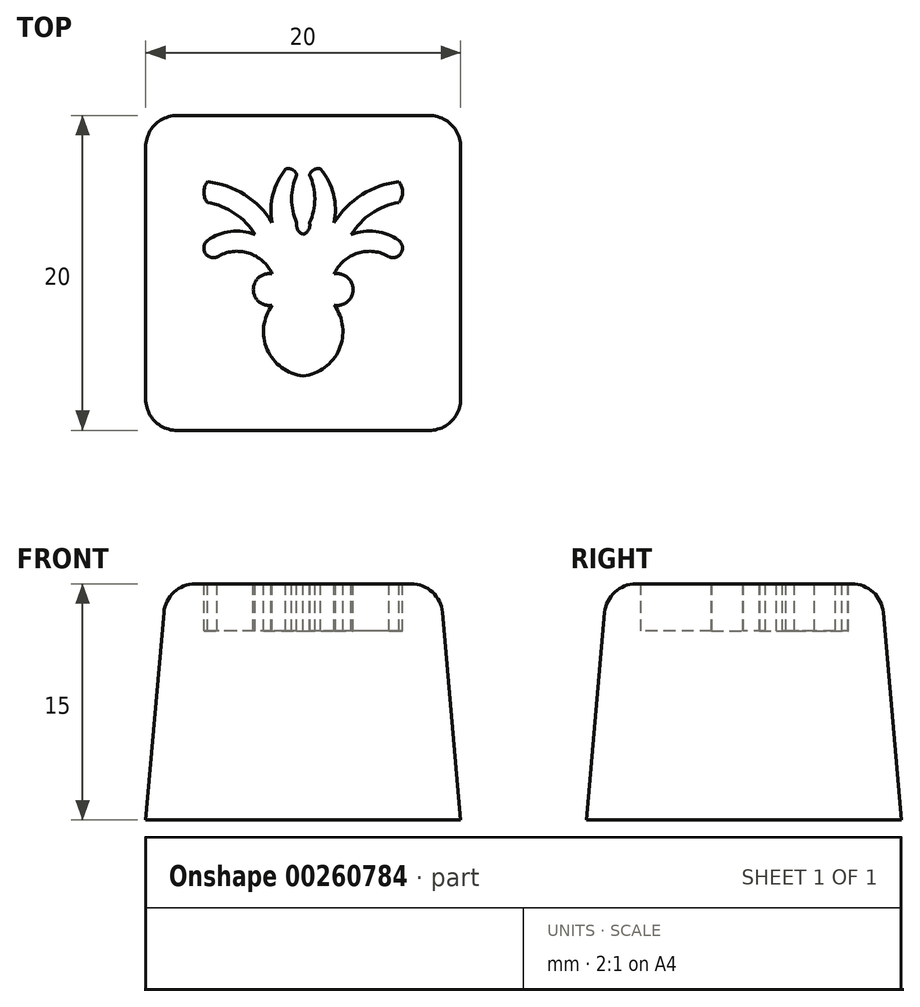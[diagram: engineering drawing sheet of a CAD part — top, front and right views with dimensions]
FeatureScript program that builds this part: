
annotation { "Feature Type Name" : "Feature", "Feature Type Description" : "" }
export const myFeature = defineFeature(function(context is Context, id is Id, definition is map)
    precondition{}
    {
        {
            var Q0;
            Q0=qCreatedBy(makeId("Top.planeOp"),FACE);
            var sketch = newSketch(context, id + "F0", { "sketchPlane" : qUnion([Q0])});
            skLineSegment(sketch, "E0.bottom", {"start": v(-8.42, 8.98) * mm, "end": v(11.58, 8.98) * mm});
            skLineSegment(sketch, "E0.top", {"start": v(-8.42, -11.02) * mm, "end": v(11.58, -11.02) * mm});
            skLineSegment(sketch, "E0.left", {"start": v(-8.42, 8.98) * mm, "end": v(-8.42, -11.02) * mm});
            skLineSegment(sketch, "E0.right", {"start": v(11.58, 8.98) * mm, "end": v(11.58, -11.02) * mm});
            skSolve(sketch);
        }
        {
            var Q0;
            Q0 = qSketchRegion(id + "F0", true);
            var Q1;
            Q1 = qSketchRegion(id + "F3", true);
            extrude(context, id + "F1", {"entities" : qUnion([Q0, Q1]), "depth" : 15 * mm, "hasDraft" : true, "draftAngle" : 5 * degree, "draftPullDirection" : true});
        }
        {
            var Q0;
            Q0=makeQuery(id+"F1.opExtrude","SWEPT_EDGE",EDGE,{"disambiguationData":[OSD([sQuery(id+"F0.wireOp",EDGE,"E0.bottom"),sQuery(id+"F0.wireOp",EDGE,"E0.left")])]});
            var Q1;
            Q1=makeQuery(id+"F1.opExtrude","CAP_EDGE",EDGE,{"disambiguationData":[OSD([sQuery(id+"F0.wireOp",EDGE,"E0.bottom")])],"isStart":false});
            var Q2;
            Q2=makeQuery(id+"F1.opExtrude","SWEPT_EDGE",EDGE,{"disambiguationData":[OSD([sQuery(id+"F0.wireOp",EDGE,"E0.bottom"),sQuery(id+"F0.wireOp",EDGE,"E0.right")])]});
            var Q3;
            Q3=makeQuery(id+"F1.opExtrude","CAP_EDGE",EDGE,{"disambiguationData":[OSD([sQuery(id+"F0.wireOp",EDGE,"E0.right")])],"isStart":false});
            var Q4;
            Q4=makeQuery(id+"F1.opExtrude","SWEPT_EDGE",EDGE,{"disambiguationData":[OSD([sQuery(id+"F0.wireOp",EDGE,"E0.top"),sQuery(id+"F0.wireOp",EDGE,"E0.right")])]});
            var Q5;
            Q5=makeQuery(id+"F1.opExtrude","CAP_EDGE",EDGE,{"disambiguationData":[OSD([sQuery(id+"F0.wireOp",EDGE,"E0.top")])],"isStart":false});
            var Q6;
            Q6=makeQuery(id+"F1.opExtrude","CAP_EDGE",EDGE,{"disambiguationData":[OSD([sQuery(id+"F0.wireOp",EDGE,"E0.left")])],"isStart":false});
            var Q7;
            Q7=makeQuery(id+"F1.opExtrude","SWEPT_EDGE",EDGE,{"disambiguationData":[OSD([sQuery(id+"F0.wireOp",EDGE,"E0.top"),sQuery(id+"F0.wireOp",EDGE,"E0.left")])]});
            fillet(context, id + "F2", {"entities" : qUnion([Q0, Q1, Q2, Q3, Q4, Q5, Q6, Q7]), "radius" : 2 * mm, "tangentPropagation" : true, "allowEdgeOverflow" : false});
        }
        {
            var Q0;
            Q0=makeQuery(id+"F1.opExtrude","CAP_FACE",FACE,{"disambiguationData":[OSD([sQuery(id+"F0.wireOp",EDGE,"E0.bottom"),sQuery(id+"F0.wireOp",EDGE,"E0.top"),sQuery(id+"F0.wireOp",EDGE,"E0.left"),sQuery(id+"F0.wireOp",EDGE,"E0.right")])],"isStart":false});
            var sketch = newSketch(context, id + "F3", { "sketchPlane" : qUnion([Q0])});
            skLineSegment(sketch, "E1", {"start": v(1.58, 5.83) * mm, "end": v(1.58, -7.88) * mm});
            skArc(sketch, "E2", {"start": v(-0.38, -3.07) * mm, "mid": v(-0.7, -5.89) * mm, "end": v(1.58, -7.56) * mm});
            skArc(sketch, "E3", {"start": v(-0.38, -1.09) * mm, "mid": v(-1.59, -2.08) * mm, "end": v(-0.38, -3.07) * mm});
            skArc(sketch, "E4", {"start": v(-0.38, -1.09) * mm, "mid": v(-1.89, 0.24) * mm, "end": v(-3.88, 0) * mm});
            skArc(sketch, "E5", {"start": v(-4.5, 1.04) * mm, "mid": v(-4.64, 0.25) * mm, "end": v(-3.88, 0) * mm});
            skArc(sketch, "E6", {"start": v(-1.47, 1.42) * mm, "mid": v(-3.03, 1.62) * mm, "end": v(-4.5, 1.04) * mm});
            skArc(sketch, "E7", {"start": v(-1.47, 1.42) * mm, "mid": v(-2.76, 2.76) * mm, "end": v(-4.5, 3.45) * mm});
            skArc(sketch, "E8", {"start": v(-4.5, 4.78) * mm, "mid": v(-4.73, 4.11) * mm, "end": v(-4.5, 3.45) * mm});
            skArc(sketch, "E9", {"start": v(-0.38, 2.18) * mm, "mid": v(-2.14, 3.95) * mm, "end": v(-4.5, 4.78) * mm});
            skArc(sketch, "E10", {"start": v(0.47, 5.58) * mm, "mid": v(-0.34, 3.97) * mm, "end": v(-0.38, 2.18) * mm});
            skArc(sketch, "E11", {"start": v(1.18, 5.2) * mm, "mid": v(0.9, 5.54) * mm, "end": v(0.47, 5.58) * mm});
            skArc(sketch, "E12", {"start": v(1.18, 5.2) * mm, "mid": v(0.85, 3.69) * mm, "end": v(1.18, 2.18) * mm});
            skArc(sketch, "E13", {"start": v(1.18, 2.18) * mm, "mid": v(1.24, 1.72) * mm, "end": v(1.58, 1.42) * mm});
            skArc(sketch, "E14.MirrorCS", {"start": v(1.99, 2.18) * mm, "mid": v(1.93, 1.72) * mm, "end": v(1.58, 1.42) * mm});
            skArc(sketch, "E15.MirrorCS", {"start": v(1.99, 5.2) * mm, "mid": v(2.32, 3.69) * mm, "end": v(1.99, 2.18) * mm});
            skArc(sketch, "E16.MirrorCS", {"start": v(1.99, 5.2) * mm, "mid": v(2.26, 5.54) * mm, "end": v(2.7, 5.58) * mm});
            skArc(sketch, "E17.MirrorCS", {"start": v(2.7, 5.58) * mm, "mid": v(3.5, 3.97) * mm, "end": v(3.55, 2.18) * mm});
            skArc(sketch, "E18.MirrorCS", {"start": v(3.55, 2.18) * mm, "mid": v(5.3, 3.95) * mm, "end": v(7.66, 4.78) * mm});
            skArc(sketch, "E19.MirrorCS", {"start": v(7.66, 4.78) * mm, "mid": v(7.9, 4.11) * mm, "end": v(7.66, 3.45) * mm});
            skArc(sketch, "E20.MirrorCS", {"start": v(4.64, 1.42) * mm, "mid": v(5.93, 2.76) * mm, "end": v(7.66, 3.45) * mm});
            skArc(sketch, "E21.MirrorCS", {"start": v(4.64, 1.42) * mm, "mid": v(6.2, 1.62) * mm, "end": v(7.66, 1.04) * mm});
            skArc(sketch, "E22.MirrorCS", {"start": v(7.66, 1.04) * mm, "mid": v(7.81, 0.25) * mm, "end": v(7.05, 0) * mm});
            skArc(sketch, "E23.MirrorCS", {"start": v(3.55, -1.09) * mm, "mid": v(5.05, 0.24) * mm, "end": v(7.05, 0) * mm});
            skArc(sketch, "E24.MirrorCS", {"start": v(3.55, -1.09) * mm, "mid": v(4.75, -2.08) * mm, "end": v(3.55, -3.07) * mm});
            skArc(sketch, "E25.MirrorCS", {"start": v(3.55, -3.07) * mm, "mid": v(3.87, -5.89) * mm, "end": v(1.58, -7.56) * mm});
            skSolve(sketch);
        }
        {
            var Q0;
            Q0 = qSketchRegion(id + "F3", true);
            extrude(context, id + "F4", {"entities" : qUnion([Q0]), "operationType" : NewBodyOperationType.REMOVE, "oppositeDirection" : true, "depth" : 3 * mm});
        }
    });
